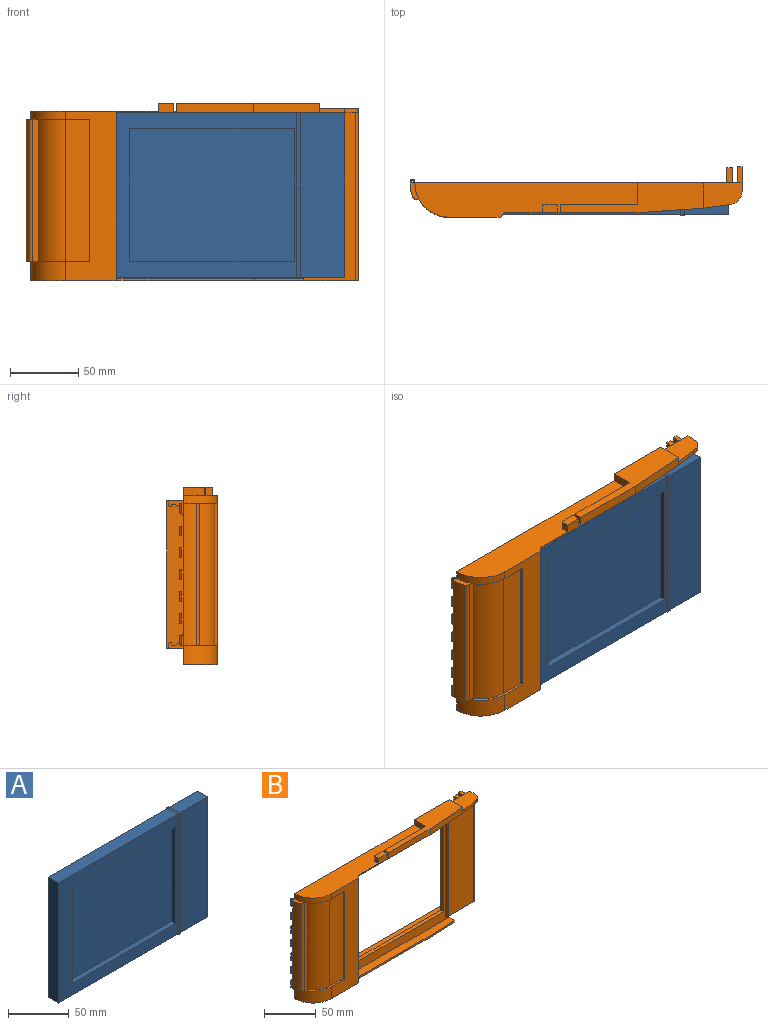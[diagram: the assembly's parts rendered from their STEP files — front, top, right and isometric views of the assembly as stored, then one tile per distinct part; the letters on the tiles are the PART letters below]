
ASSEMBLY  parts=2 mates=1
PART A: 32 faces, bbox 173x13.8x120.5 mm
  f0: plane 173x120.5mm, normal (0,-1,0), area 8885.9mm2, adj f1,f2,f3,f7,f8,f9,f10,f11
  f1: plane 120.2x4.7mm, normal (0,0,1), area 564.9mm2, adj f0,f2,f12,f19
  f2: plane 97x4.7mm, normal (1,0,0), area 455.9mm2, adj f0,f1,f3,f19
  f3: plane 120.2x4.7mm, normal (0,0,-1), area 564.9mm2, adj f0,f2,f12,f19
  f4: plane 11.8x0.03mm, normal (1,0,0), area 0.4mm2, adj f5,f11,f13,f25
  f5: plane 11.8x2.5mm, normal (0,0,1), area 29.5mm2, adj f4,f6,f13,f25
  f6: plane 11.8x0.03mm, normal (-1,0,0), area 0.4mm2, adj f5,f7,f13,f25
  f7: plane 138x11.8mm, normal (0,0,1), area 1628.4mm2, adj f0,f6,f8,f20
  f8: plane 120.5x11.8mm, normal (-1,0,0), area 1421.9mm2, adj f0,f7,f9,f20
  f9: plane 173x11.8mm, normal (0,0,-1), area 2041.4mm2, adj f0,f8,f10,f20
  f10: plane 120.5x11.8mm, normal (1,0,0), area 1421.9mm2, adj f0,f9,f11,f20
  f11: plane 32.5x11.8mm, normal (0,0,1), area 383.5mm2, adj f0,f4,f10,f20
  f12: plane 97x4.7mm, normal (-1,0,0), area 455.9mm2, adj f0,f1,f3,f19
  f13: plane 2.5x0.03mm, normal (0,-1,0), area 0.1mm2, adj f4,f5,f6,f17
  f14: plane 120.47x1mm, normal (-1,0,0), area 120.5mm2, adj f0,f15,f17,f18
  f15: plane 2.5x1mm, normal (0,0,-1), area 2.5mm2, adj f0,f14,f16,f18
  f16: plane 120.47x1mm, normal (1,0,0), area 120.5mm2, adj f0,f15,f17,f18
  f17: plane 2.5x1mm, normal (0,0,1), area 2.5mm2, adj f13,f14,f16,f18
  f18: plane 120.47x2.5mm, normal (0,-1,0), area 301.2mm2, adj f14,f15,f16,f17
  f19: plane 120.2x97mm, normal (0,-1,0), area 11659.4mm2, adj f1,f2,f3,f12
  f20: plane 173x120.5mm, normal (0,1,0), area 8885.9mm2, adj f7,f8,f9,f10,f11,f21,f22,f23
  f21: plane 120.2x4.7mm, normal (0,0,1), area 564.9mm2, adj f20,f22,f24,f31
  f22: plane 97x4.7mm, normal (1,0,0), area 455.9mm2, adj f20,f21,f23,f31
  f23: plane 120.2x4.7mm, normal (0,0,-1), area 564.9mm2, adj f20,f22,f24,f31
  f24: plane 97x4.7mm, normal (-1,0,0), area 455.9mm2, adj f20,f21,f23,f31
  f25: plane 2.5x0.03mm, normal (0,1,0), area 0.1mm2, adj f4,f5,f6,f29
  f26: plane 120.47x1mm, normal (-1,0,0), area 120.5mm2, adj f20,f27,f29,f30
  f27: plane 2.5x1mm, normal (0,0,-1), area 2.5mm2, adj f20,f26,f28,f30
  f28: plane 120.47x1mm, normal (1,0,0), area 120.5mm2, adj f20,f27,f29,f30
  f29: plane 2.5x1mm, normal (0,0,1), area 2.5mm2, adj f25,f26,f28,f30
  f30: plane 120.47x2.5mm, normal (0,1,0), area 301.2mm2, adj f26,f27,f28,f29
  f31: plane 120.2x97mm, normal (0,1,0), area 11659.4mm2, adj f21,f22,f23,f24
PART B: 171 faces, bbox 242.6x37x130 mm
  f0: plane 112x43.28mm, normal (0,1,0), area 4742.8mm2, adj f26,f32,f33,f49,f148,f149,f155,f156
  f1: plane 7.5x1mm, normal (1,0,0), area 7.5mm2, adj f16,f44,f101,f145
  f2: plane 7x1mm, normal (1,0,0), area 7mm2, adj f17,f44,f137,f146
  f3: plane 7x1mm, normal (1,0,0), area 7mm2, adj f18,f44,f129,f138
  f4: plane 7x1mm, normal (1,0,0), area 7mm2, adj f19,f44,f121,f130
  f5: plane 7x1mm, normal (1,0,0), area 7mm2, adj f20,f44,f113,f122
  f6: plane 7x1mm, normal (1,0,0), area 7mm2, adj f21,f44,f105,f114
  f7: plane 7x1mm, normal (-1,0,0), area 7mm2, adj f17,f98,f137,f146
  f8: plane 7x1mm, normal (-1,0,0), area 7mm2, adj f18,f98,f129,f138
  f9: plane 7x1mm, normal (-1,0,0), area 7mm2, adj f19,f98,f121,f130
  f10: plane 7x1mm, normal (-1,0,0), area 7mm2, adj f20,f98,f113,f122
  f11: plane 7x1mm, normal (-1,0,0), area 7mm2, adj f21,f98,f105,f114
  f12: plane 7.5x1mm, normal (-1,0,0), area 7.5mm2, adj f96,f98,f102,f106
  f13: plane 7.5x1mm, normal (1,0,0), area 7.5mm2, adj f14,f22,f102,f106
  f14: cylinder r=1mm len=7.5mm, axis (0,0,1), area 23.6mm2, adj f13,f15,f102,f106
  f15: plane 7.5x1mm, normal (-1,0,0), area 7.5mm2, adj f14,f22,f102,f106
  f16: cylinder r=1.8mm len=7.5mm, axis (0,0,1), area 42.4mm2, adj f1,f97,f101,f145
  f17: cylinder r=1.8mm len=7mm, axis (0,0,1), area 39.6mm2, adj f2,f7,f137,f146
  f18: cylinder r=1.8mm len=7mm, axis (0,0,1), area 39.6mm2, adj f3,f8,f129,f138
  f19: cylinder r=1.8mm len=7mm, axis (0,0,1), area 39.6mm2, adj f4,f9,f121,f130
  f20: cylinder r=1.8mm len=7mm, axis (0,0,1), area 39.6mm2, adj f5,f10,f113,f122
  f21: cylinder r=1.8mm len=7mm, axis (0,0,1), area 39.6mm2, adj f6,f11,f105,f114
  f22: plane 7.5x2mm, normal (0,1,0), area 15mm2, adj f13,f15,f102,f106
  f23: cylinder r=25mm len=25mm, axis (0,0,-1), area 549.8mm2, adj f40,f43,f44,f48,f102
  f24: plane 183.6x19.5mm, normal (0,0,-1), area 1886.7mm2, adj f27,f28,f35,f36,f37,f38,f45,f47
  f25: plane 144x15.8mm, normal (0,0,1), area 1306mm2, adj f27,f28,f36,f37,f38,f75,f76,f77
  f26: plane 234x21mm, normal (0,0,1), area 2193.9mm2, adj f0,f29,f30,f31,f33,f44,f49,f50
  f27: plane 121x2.6mm, normal (0,-1,0), area 300.8mm2, adj f24,f25,f87,f90
  f28: plane 121x0.33mm, normal (0,-1,0), area 39.6mm2, adj f24,f25,f36,f86
  f29: plane 112x2.33mm, normal (0,1,0), area 260.7mm2, adj f26,f32,f54,f89
  f30: plane 112x5mm, normal (-1,0,0), area 560mm2, adj f26,f32,f55,f88
  f31: plane 112x5mm, normal (1,0,0), area 560mm2, adj f26,f32,f55,f83
  f32: plane 234x21mm, normal (0,0,-1), area 2193.9mm2, adj f0,f29,f30,f31,f33,f44,f49,f50
  f33: plane 112x1mm, normal (-1,0,0), area 112mm2, adj f0,f26,f32,f83
  f34: plane 15.7x6mm, normal (-1,0,0), area 94.2mm2, adj f44,f63,f67,f70
  f35: plane 123x37.6mm, normal (0,-1,0), area 4624.8mm2, adj f24,f48,f78,f79
  f36: plane 121x13.8mm, normal (1,0,0), area 1669.7mm2, adj f24,f25,f28,f38
  f37: plane 121x2mm, normal (1,0,0), area 242.1mm2, adj f24,f25,f38,f43
  f38: plane 121x6.8mm, normal (0,1,0), area 822.8mm2, adj f24,f25,f36,f37
  f39: plane 104x4.34mm, normal (0,-1,0), area 451.8mm2, adj f40,f41,f59,f99,f101,f102
  f40: plane 39.93x13mm, normal (0,0,1), area 86.3mm2, adj f23,f39,f42,f43,f59,f60
  f41: plane 39.93x13mm, normal (0,0,-1), area 86.3mm2, adj f39,f42,f43,f46,f59,f60
  f42: plane 104x2mm, normal (-1,0,0), area 208mm2, adj f40,f41,f43,f60
  f43: plane 124x37.2mm, normal (0,-1,0), area 2740.8mm2, adj f23,f37,f40,f41,f42,f46,f48,f61
  f44: plane 239x130mm, normal (0,1,0), area 3448mm2, adj f1,f2,f3,f4,f5,f6,f23,f26
  f45: plane 126x18mm, normal (1,0,0), area 1990.5mm2, adj f24,f44,f47,f48,f56,f57,f58,f65
  f46: cylinder r=25mm len=25mm, axis (0,0,-1), area 235.6mm2, adj f41,f43,f44,f63,f101
  f47: cylinder r=10mm len=10mm, axis (0,0,-1), area 47.1mm2, adj f24,f45,f64,f65
  f48: plane 239x25mm, normal (0,0,-1), area 4445.7mm2, adj f23,f35,f43,f44,f45,f75,f76,f77
  f49: plane 112x18mm, normal (-1,0,0), area 1968mm2, adj f0,f26,f32,f44,f56,f57,f58
  f50: cylinder r=23mm len=112mm, axis (0,0,-1), area 1158.7mm2, adj f26,f32,f44,f51
  f51: plane 112x2.25mm, normal (0,1,0), area 251.6mm2, adj f26,f32,f50,f52
  f52: cylinder r=21mm len=112mm, axis (0,0,-1), area 2527.2mm2, adj f26,f32,f51,f53
  f53: plane 112x28.4mm, normal (0,1,0), area 3180.8mm2, adj f26,f32,f52,f54
  f54: plane 112x13.8mm, normal (-1,0,0), area 1545.6mm2, adj f26,f29,f32,f53
  f55: plane 112x1mm, normal (0,1,0), area 112mm2, adj f26,f30,f31,f32
  f56: plane 108x3mm, normal (0,1,0), area 324mm2, adj f45,f49,f57,f58
  f57: plane 12x3mm, normal (0,0,1), area 36mm2, adj f44,f45,f49,f56
  f58: plane 12x3mm, normal (0,0,-1), area 36mm2, adj f44,f45,f49,f56
  f59: cylinder r=23mm len=104mm, axis (0,0,-1), area 2444.4mm2, adj f39,f40,f41,f60
  f60: plane 104x18mm, normal (0,-1,0), area 1872mm2, adj f40,f41,f42,f59
  f61: plane 3.3x3.3mm, normal (0.71,-0.71,0), area 4.7mm2, adj f24,f43,f62,f63
  f62: plane 97.5x7mm, normal (0,-1,0), area 505.5mm2, adj f24,f61,f63,f68,f69,f70,f72,f73
  f63: plane 163x25mm, normal (0,0,1), area 3206.1mm2, adj f34,f43,f44,f46,f61,f62,f67,f68
  f64: plane 18x3mm, normal (0.14,-0.99,0), area 54.5mm2, adj f24,f47,f65,f69
  f65: plane 28x18.45mm, normal (0,0,1), area 448.6mm2, adj f44,f45,f47,f64,f66
  f66: plane 18.45x4mm, normal (1,0,0), area 73.8mm2, adj f44,f65,f69,f70
  f67: plane 56.5x6mm, normal (0,1,0), area 339mm2, adj f34,f63,f68,f70
  f68: plane 6x6mm, normal (-1,0,0), area 36mm2, adj f62,f63,f67,f70
  f69: plane 48x7mm, normal (0.07,-1,0), area 336.8mm2, adj f24,f62,f64,f66,f70
  f70: plane 104.5x21.7mm, normal (0,0,1), area 1302.7mm2, adj f34,f44,f62,f66,f67,f68,f69
  f71: plane 9.5x6mm, normal (0,1,0), area 57mm2, adj f63,f74,f169,f170
  f72: plane 6x5mm, normal (-1,0,0), area 30mm2, adj f62,f63,f74,f170
  f73: plane 6x5mm, normal (1,0,0), area 30mm2, adj f62,f63,f74,f169
  f74: plane 11.5x6mm, normal (0,0,1), area 68.6mm2, adj f62,f71,f72,f73,f169,f170
  f75: plane 5x5mm, normal (0.71,-0.71,0), area 14.1mm2, adj f25,f43,f48,f76
  f76: plane 96.16x2mm, normal (0,-1,0), area 192.3mm2, adj f25,f48,f75,f77
  f77: plane 36.04x2mm, normal (0.04,-1,0), area 72.1mm2, adj f25,f48,f76,f78
  f78: plane 123x10.95mm, normal (1,0,0), area 445.4mm2, adj f24,f25,f35,f48,f77,f91
  f79: cylinder r=2mm len=123mm, axis (0,0,1), area 386.4mm2, adj f24,f35,f45,f48
  f80: plane 122.77x4mm, normal (0,0,-1), area 491.1mm2, adj f81,f83,f84,f85
  f81: plane 107x4mm, normal (1,0,0), area 428mm2, adj f80,f82,f83,f85
  f82: plane 122.77x4mm, normal (0,0,1), area 491.1mm2, adj f81,f83,f84,f85
  f83: plane 125.23x112mm, normal (0,1,0), area 888.5mm2, adj f26,f31,f32,f33,f80,f81,f82,f84
  f84: plane 107x4mm, normal (-1,0,0), area 428mm2, adj f80,f82,f83,f85
  f85: plane 138.8x121mm, normal (0,-1,0), area 3644.4mm2, adj f24,f25,f80,f81,f82,f84,f86,f87
  f86: plane 121x1.8mm, normal (-1,0,0), area 217.8mm2, adj f24,f25,f28,f85
  f87: plane 121x1.8mm, normal (1,0,0), area 217.8mm2, adj f24,f25,f27,f85
  f88: plane 112x10.77mm, normal (0,1,0), area 1206.5mm2, adj f26,f30,f32,f89
  f89: plane 112x0.2mm, normal (-1,0,0), area 22.4mm2, adj f26,f29,f32,f88
  f90: plane 121x1.8mm, normal (-1,0,0), area 217.8mm2, adj f24,f25,f27,f91
  f91: plane 121x2.5mm, normal (0,-1,0), area 302.5mm2, adj f24,f25,f78,f90
  f92: plane 7.5x1mm, normal (1,0,0), area 7.5mm2, adj f93,f100,f101,f145
  f93: cylinder r=1mm len=7.5mm, axis (0,0,1), area 23.6mm2, adj f92,f94,f101,f145
  f94: plane 7.5x1mm, normal (-1,0,0), area 7.5mm2, adj f93,f100,f101,f145
  f95: plane 7.5x1mm, normal (1,0,0), area 7.5mm2, adj f44,f96,f102,f106
  f96: cylinder r=1.8mm len=7.5mm, axis (0,0,1), area 42.4mm2, adj f12,f95,f102,f106
  f97: plane 7.5x1mm, normal (-1,0,0), area 7.5mm2, adj f16,f98,f101,f145
  f98: cylinder r=28.6mm len=104mm, axis (0,0,1), area 1037mm2, adj f7,f8,f9,f10,f11,f12,f97,f99
  f99: cylinder r=3mm len=104mm, axis (0,0,1), area 378mm2, adj f39,f98,f101,f102
  f100: plane 7.5x2mm, normal (0,1,0), area 15mm2, adj f92,f94,f101,f145
  f101: plane 14.8x6.67mm, normal (0,0,1), area 49.2mm2, adj f1,f16,f39,f46,f92,f93,f94,f97
  f102: plane 14.8x6.67mm, normal (0,0,-1), area 49.2mm2, adj f12,f13,f14,f15,f22,f23,f39,f95
  f103: cylinder r=25mm len=9mm, axis (0,0,-1), area 5.2mm2, adj f44,f104,f105,f106
  f104: plane 9x3.6mm, normal (0,1,0), area 32.4mm2, adj f98,f103,f105,f106
  f105: plane 3.61x3.38mm, normal (0,0,-1), area 7.2mm2, adj f6,f11,f21,f98,f103,f104,f107,f108
  f106: plane 3.61x3.38mm, normal (0,0,1), area 7.2mm2, adj f12,f13,f14,f15,f22,f95,f96,f98
  f107: plane 7x2mm, normal (0,1,0), area 14mm2, adj f105,f108,f110,f114
  f108: plane 7x1mm, normal (-1,0,0), area 7mm2, adj f105,f107,f109,f114
  f109: cylinder r=1mm len=7mm, axis (0,0,1), area 22mm2, adj f105,f108,f110,f114
  f110: plane 7x1mm, normal (1,0,0), area 7mm2, adj f105,f107,f109,f114
  f111: cylinder r=25mm len=9mm, axis (0,0,-1), area 5.2mm2, adj f44,f112,f113,f114
  f112: plane 9x3.6mm, normal (0,1,0), area 32.4mm2, adj f98,f111,f113,f114
  f113: plane 3.61x3.38mm, normal (0,0,-1), area 7.2mm2, adj f5,f10,f20,f98,f111,f112,f115,f116
  f114: plane 3.61x3.38mm, normal (0,0,1), area 7.2mm2, adj f6,f11,f21,f98,f107,f108,f109,f110
  f115: plane 7x2mm, normal (0,1,0), area 14mm2, adj f113,f116,f118,f122
  f116: plane 7x1mm, normal (-1,0,0), area 7mm2, adj f113,f115,f117,f122
  f117: cylinder r=1mm len=7mm, axis (0,0,1), area 22mm2, adj f113,f116,f118,f122
  f118: plane 7x1mm, normal (1,0,0), area 7mm2, adj f113,f115,f117,f122
  f119: cylinder r=25mm len=9mm, axis (0,0,-1), area 5.2mm2, adj f44,f120,f121,f122
  f120: plane 9x3.6mm, normal (0,1,0), area 32.4mm2, adj f98,f119,f121,f122
  f121: plane 3.61x3.38mm, normal (0,0,-1), area 7.2mm2, adj f4,f9,f19,f98,f119,f120,f123,f124
  f122: plane 3.61x3.38mm, normal (0,0,1), area 7.2mm2, adj f5,f10,f20,f98,f115,f116,f117,f118
  f123: plane 7x2mm, normal (0,1,0), area 14mm2, adj f121,f124,f126,f130
  f124: plane 7x1mm, normal (-1,0,0), area 7mm2, adj f121,f123,f125,f130
  f125: cylinder r=1mm len=7mm, axis (0,0,1), area 22mm2, adj f121,f124,f126,f130
  f126: plane 7x1mm, normal (1,0,0), area 7mm2, adj f121,f123,f125,f130
  f127: cylinder r=25mm len=9mm, axis (0,0,-1), area 5.2mm2, adj f44,f128,f129,f130
  f128: plane 9x3.6mm, normal (0,1,0), area 32.4mm2, adj f98,f127,f129,f130
  f129: plane 3.61x3.38mm, normal (0,0,-1), area 7.2mm2, adj f3,f8,f18,f98,f127,f128,f131,f132
  f130: plane 3.61x3.38mm, normal (0,0,1), area 7.2mm2, adj f4,f9,f19,f98,f123,f124,f125,f126
  f131: plane 7x2mm, normal (0,1,0), area 14mm2, adj f129,f132,f134,f138
  f132: plane 7x1mm, normal (-1,0,0), area 7mm2, adj f129,f131,f133,f138
  f133: cylinder r=1mm len=7mm, axis (0,0,1), area 22mm2, adj f129,f132,f134,f138
  f134: plane 7x1mm, normal (1,0,0), area 7mm2, adj f129,f131,f133,f138
  f135: cylinder r=25mm len=9mm, axis (0,0,-1), area 5.2mm2, adj f44,f136,f137,f138
  f136: plane 9x3.6mm, normal (0,1,0), area 32.4mm2, adj f98,f135,f137,f138
  f137: plane 3.61x3.38mm, normal (0,0,-1), area 7.2mm2, adj f2,f7,f17,f98,f135,f136,f139,f140
  f138: plane 3.61x3.38mm, normal (0,0,1), area 7.2mm2, adj f3,f8,f18,f98,f131,f132,f133,f134
  f139: plane 7x2mm, normal (0,1,0), area 14mm2, adj f137,f140,f142,f146
  f140: plane 7x1mm, normal (-1,0,0), area 7mm2, adj f137,f139,f141,f146
  f141: cylinder r=1mm len=7mm, axis (0,0,1), area 22mm2, adj f137,f140,f142,f146
  f142: plane 7x1mm, normal (1,0,0), area 7mm2, adj f137,f139,f141,f146
  f143: cylinder r=25mm len=9mm, axis (0,0,-1), area 5.2mm2, adj f44,f144,f145,f146
  f144: plane 9x3.6mm, normal (0,1,0), area 32.4mm2, adj f98,f143,f145,f146
  f145: plane 3.61x3.38mm, normal (0,0,-1), area 7.2mm2, adj f1,f16,f92,f93,f94,f97,f98,f100
  f146: plane 3.61x3.38mm, normal (0,0,1), area 7.2mm2, adj f2,f7,f17,f98,f139,f140,f141,f142
  f147: plane 4x3.5mm, normal (0,1,0), area 14mm2, adj f148,f155,f156,f168
  f148: plane 17x4mm, normal (0,0,1), area 68mm2, adj f0,f147,f155,f156
  f149: plane 5.09x4mm, normal (0,0,-1), area 20.4mm2, adj f0,f150,f155,f156
  f150: plane 8x4mm, normal (0,0.92,-0.39), area 34.8mm2, adj f149,f151,f155,f156
  f151: plane 4x3mm, normal (0,0.64,-0.77), area 15.6mm2, adj f150,f152,f155,f156
  f152: plane 4x3mm, normal (0,0,-1), area 12mm2, adj f151,f153,f155,f156
  f153: plane 4x2mm, normal (0,-1,0), area 8mm2, adj f152,f154,f155,f156
  f154: plane 4x1.5mm, normal (0,0,-1), area 6mm2, adj f153,f155,f156,f168
  f155: plane 17x13mm, normal (1,0,0), area 126.4mm2, adj f0,f147,f148,f149,f150,f151,f152,f153
  f156: plane 17x13mm, normal (-1,0,0), area 126.4mm2, adj f0,f147,f148,f149,f150,f151,f152,f153
  f157: plane 4x3.5mm, normal (0,1,0), area 14mm2, adj f158,f165,f166,f167
  f158: plane 17x4mm, normal (0,0,-1), area 68mm2, adj f0,f157,f165,f166
  f159: plane 5.09x4mm, normal (0,0,1), area 20.4mm2, adj f0,f160,f165,f166
  f160: plane 8x4mm, normal (0,0.92,0.39), area 34.8mm2, adj f159,f161,f165,f166
  f161: plane 4x3mm, normal (0,0.64,0.77), area 15.6mm2, adj f160,f162,f165,f166
  f162: plane 4x3mm, normal (0,0,1), area 12mm2, adj f161,f163,f165,f166
  f163: plane 4x2mm, normal (0,-1,0), area 8mm2, adj f162,f164,f165,f166
  f164: plane 4x1.5mm, normal (0,0,1), area 6mm2, adj f163,f165,f166,f167
  f165: plane 17x13mm, normal (1,0,0), area 126.4mm2, adj f0,f157,f158,f159,f160,f161,f162,f163
  f166: plane 17x13mm, normal (-1,0,0), area 126.4mm2, adj f0,f157,f158,f159,f160,f161,f162,f163
  f167: plane 4x1mm, normal (0,0.71,0.71), area 5.7mm2, adj f157,f164,f165,f166
  f168: plane 4x1mm, normal (0,0.71,-0.71), area 5.7mm2, adj f147,f154,f155,f156
  f169: cylinder r=1mm len=6mm, axis (0,0,1), area 9.4mm2, adj f63,f71,f73,f74
  f170: cylinder r=1mm len=6mm, axis (0,0,1), area 9.4mm2, adj f63,f71,f72,f74
PLACE A t=(22.78,-10.26,-6.12)mm
PLACE B t=(-12.11,-18.36,-2.87)mm fixed
MATE slider A.f8 <-> B.f86  axis (1,0,0) through (-63.72,-4.36,54.13)mm
